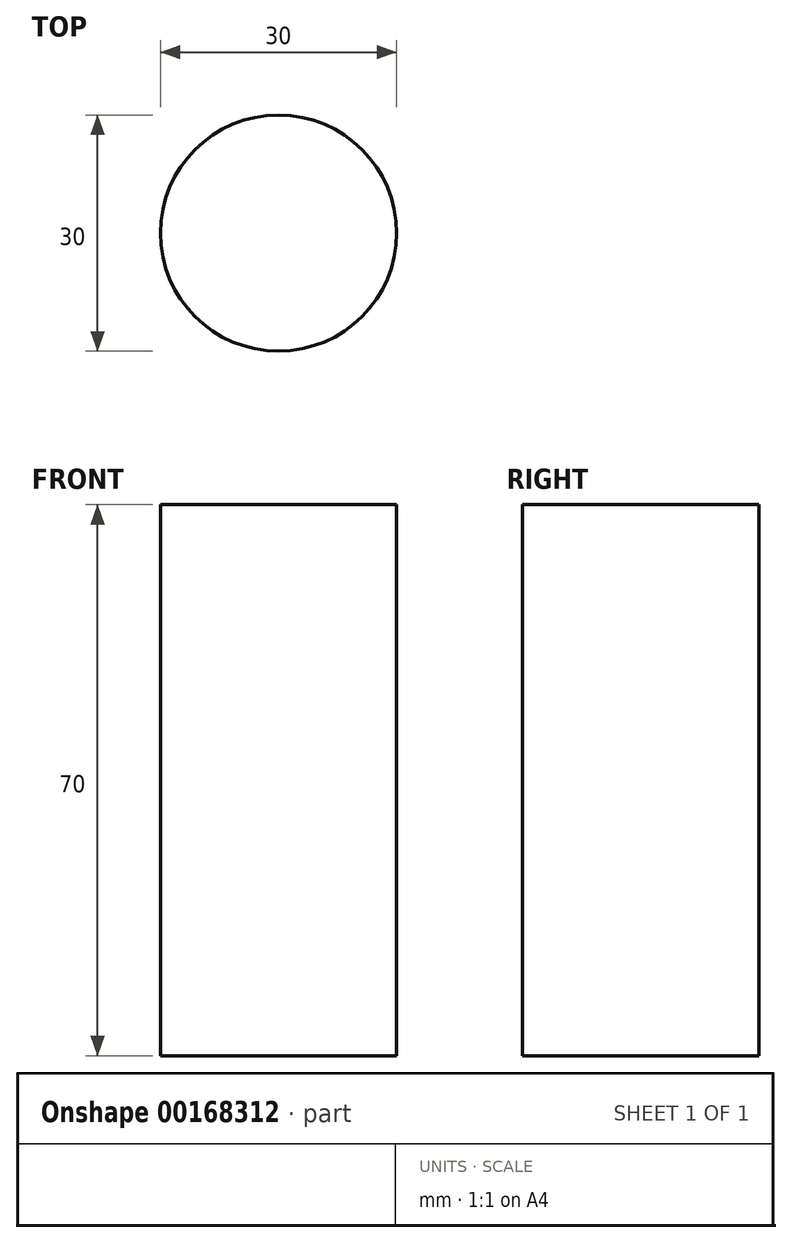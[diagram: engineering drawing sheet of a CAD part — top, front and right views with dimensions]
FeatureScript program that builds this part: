
annotation { "Feature Type Name" : "Feature", "Feature Type Description" : "" }
export const myFeature = defineFeature(function(context is Context, id is Id, definition is map)
    precondition{}
    {
        {
            var Q0;
            Q0=qCreatedBy(makeId("Top.planeOp"),FACE);
            var sketch = newSketch(context, id + "F0", { "sketchPlane" : qUnion([Q0])});
            skCircle(sketch, "E0", {"center": v(0, 0) * mm, "radius": 15 * mm});
            skSolve(sketch);
        }
        {
            var Q0;
            Q0=qSketchRegion(id+"F0",true);
            extrude(context, id + "F1", {"entities" : qUnion([Q0]), "depth" : 70 * mm});
        }
    });
